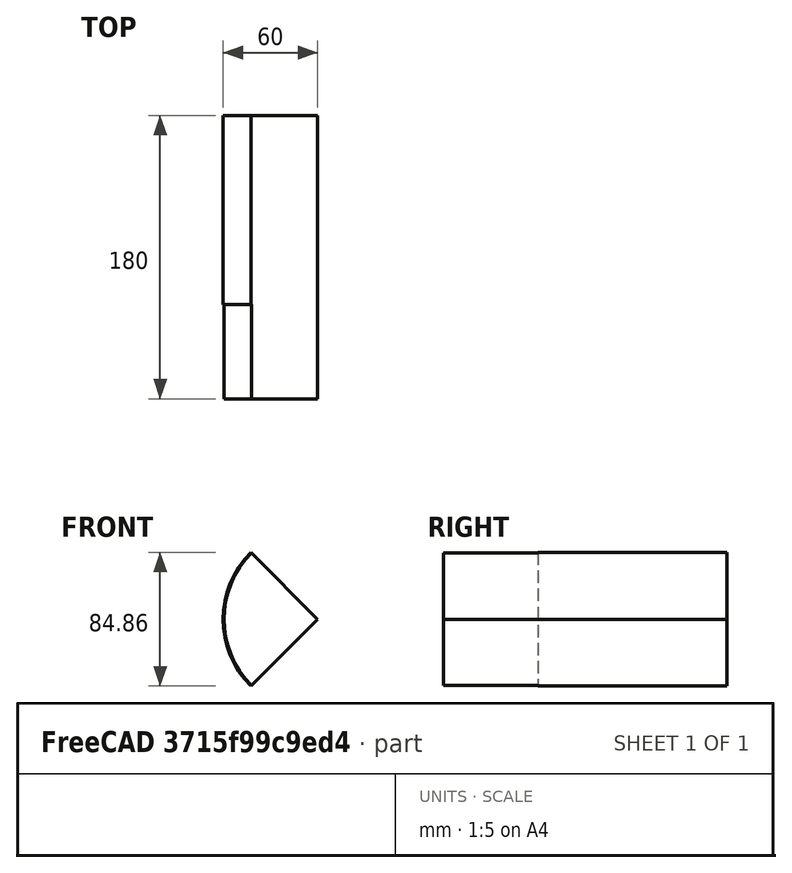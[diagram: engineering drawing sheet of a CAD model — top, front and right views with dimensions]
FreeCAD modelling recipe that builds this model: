
FCSTD DOCUMENT  (FreeCAD 1.2R20260217 (Git shallow))
Label: freeCAD_final
License: All rights reserved
LicenseURL: https://en.wikipedia.org/wiki/All_rights_reserved
objects: PartDesign::Pad×3, Fem::FeaturePython×3, Sketcher::SketchObject×2, App::Point×1, PartDesign::Body×1, Fem::FemMeshShapeBaseObjectPython×1, Mesh::Feature×1
note: 14 computed .brp shape members not serialized (recipe doc carries the construction recipe); baked Part::Feature solids carry a one-line shape summary decoded from their .brp

FEATURE [App::Point] Origin001
  Role = Origin
FEATURE [Sketcher::SketchObject] Sketch
  ArcFitTolerance = 1e-06
  AttachmentSupport = -> [Origin]
  ExternalTypes = [0]
  FullyConstrained = true
  MakeInternals = false
  MapMode = 5
  Placement = pos=(0,0,0) rot=(1,0,0;1.5708rad)
  sketch-geometry (3):
    g0: ArcOfCircle CenterX=0 CenterY=0 CenterZ=0 NormalX=0 NormalY=0 NormalZ=1 AngleXU=0 Radius=60 StartAngle=2.35619 EndAngle=3.92699
    g1: LineSegment StartX=-42.4264 StartY=42.4264 StartZ=0 EndX=-3.2e-15 EndY=-3e-15 EndZ=0
    g2: LineSegment StartX=-42.4264 StartY=-42.4264 StartZ=0 EndX=7.2e-15 EndY=5.9e-15 EndZ=0
  constraints (11):
    c: Radius(g0) = 60
    c: PointOnObject(g0,g-1)
    c: PointOnObject(g0,g-2)
    c: PointOnObject(g1,g-2)
    c: Coincident(g2,g0)
    c: PointOnObject(g2,g-2)
    c: PointOnObject(g2,g-1)
    c: PointOnObject(g0,g1)
    c: Coincident(g1,g0)
    c: Angle(g-2,g1) = 0.785398
    c: Angle(g2,g-2) = 0.785398
FEATURE [PartDesign::Pad] Pad
  Direction = (0,-1,2e-16)
  Length = 10
  Length2 = 10
  Profile = -> Sketch
  ReferenceAxis = -> Sketch [N_Axis]
  Refine = true
  SideType = 0
  Suppressed = false
  Type = 0
  Type2 = 0
FEATURE [PartDesign::Pad] Pad001
  BaseFeature = -> Pad
  Direction = (0,-1,2e-16)
  Length = 120
  Length2 = 10
  Profile = -> Sketch
  ReferenceAxis = -> Sketch [N_Axis]
  Refine = true
  SideType = 0
  Suppressed = false
  Type = 0
  Type2 = 0
FEATURE [Sketcher::SketchObject] Sketch002
  ArcFitTolerance = 1e-06
  AttachmentSupport = -> [Pad001]
  ExternalTypes = [0]
  FullyConstrained = true
  MakeInternals = false
  MapMode = 5
  Placement = pos=(0,-120,0) rot=(1,0,0;1.5708rad)
  sketch-geometry (3):
    g0: ArcOfCircle CenterX=2.4e-15 CenterY=2e-15 CenterZ=0 NormalX=0 NormalY=0 NormalZ=1 AngleXU=0 Radius=59.5 StartAngle=2.35619 EndAngle=3.92699
    g1: LineSegment StartX=2.4e-15 StartY=2e-15 StartZ=0 EndX=-42.0728 EndY=42.0729 EndZ=0
    g2: LineSegment StartX=-42.0728 StartY=-42.0729 StartZ=0 EndX=2.4e-15 EndY=2e-15 EndZ=0
  constraints (8):
    c: Radius(g0) = 59.5
    c: Coincident(g0,g-1)
    c: Coincident(g1,g0)
    c: Coincident(g1,g0)
    c: Coincident(g2,g0)
    c: Coincident(g2,g0)
    c: Angle(g-2,g1) = 0.785398
    c: Angle(g2,g-2) = 0.785398
FEATURE [PartDesign::Pad] Pad002
  BaseFeature = -> Pad001
  Direction = (0,-1,2e-16)
  Length = 60
  Length2 = 10
  Profile = -> Sketch002
  ReferenceAxis = -> Sketch002 [N_Axis]
  Refine = true
  SideType = 0
  Suppressed = false
  Type = 0
  Type2 = 0
FEATURE [PartDesign::Body] Body
  AllowCompound = true
  Group = -> [Sketch,Pad,Pad001,Sketch002,Pad002]
  Origin = -> Origin
  Tip = -> Pad002
FEATURE [Fem::FeaturePython] MeshGroup  label="inlet"  # FEM object (typed FeaturePython)
  References = -> [Pad002]
  Suppressed = false
  UseLabel = true
FEATURE [Fem::FeaturePython] MeshGroup001  label="outlet"  # FEM object (typed FeaturePython)
  References = -> [Pad002]
  Suppressed = false
  UseLabel = true
FEATURE [Fem::FeaturePython] MeshGroup002  label="symm"  # FEM object (typed FeaturePython)
  References = -> [Pad002]
  Suppressed = false
  UseLabel = true
FEATURE [Fem::FemMeshShapeBaseObjectPython] FEMMeshGmsh  label="FEMMeshGmsh001"  # FEM object (typed FeaturePython)
  Algorithm2D = 0
  Algorithm3D = 0
  CharacteristicLengthMax = 10
  CharacteristicLengthMin = 10
  CoherenceMesh = true
  ElementDimension = 3
  ElementOrder = 0
  GeometryTolerance = 0
  GroupsOfNodes = true
  HighOrderOptimize = 0
  MeshGroupList = -> [MeshGroup,MeshGroup001,MeshGroup002]
  MeshSizeFromCurvature = 0
  OptimizeNetgen = true
  OptimizeStd = true
  RecombinationAlgorithm = 0
  Recombine3DAll = false
  RecombineAll = false
  SecondOrderLinear = false
  Shape = -> Pad002
  SubdivisionAlgorithm = 2
  Suppressed = false
FEATURE [Mesh::Feature] Mesh  label="Body (Meshed)"
